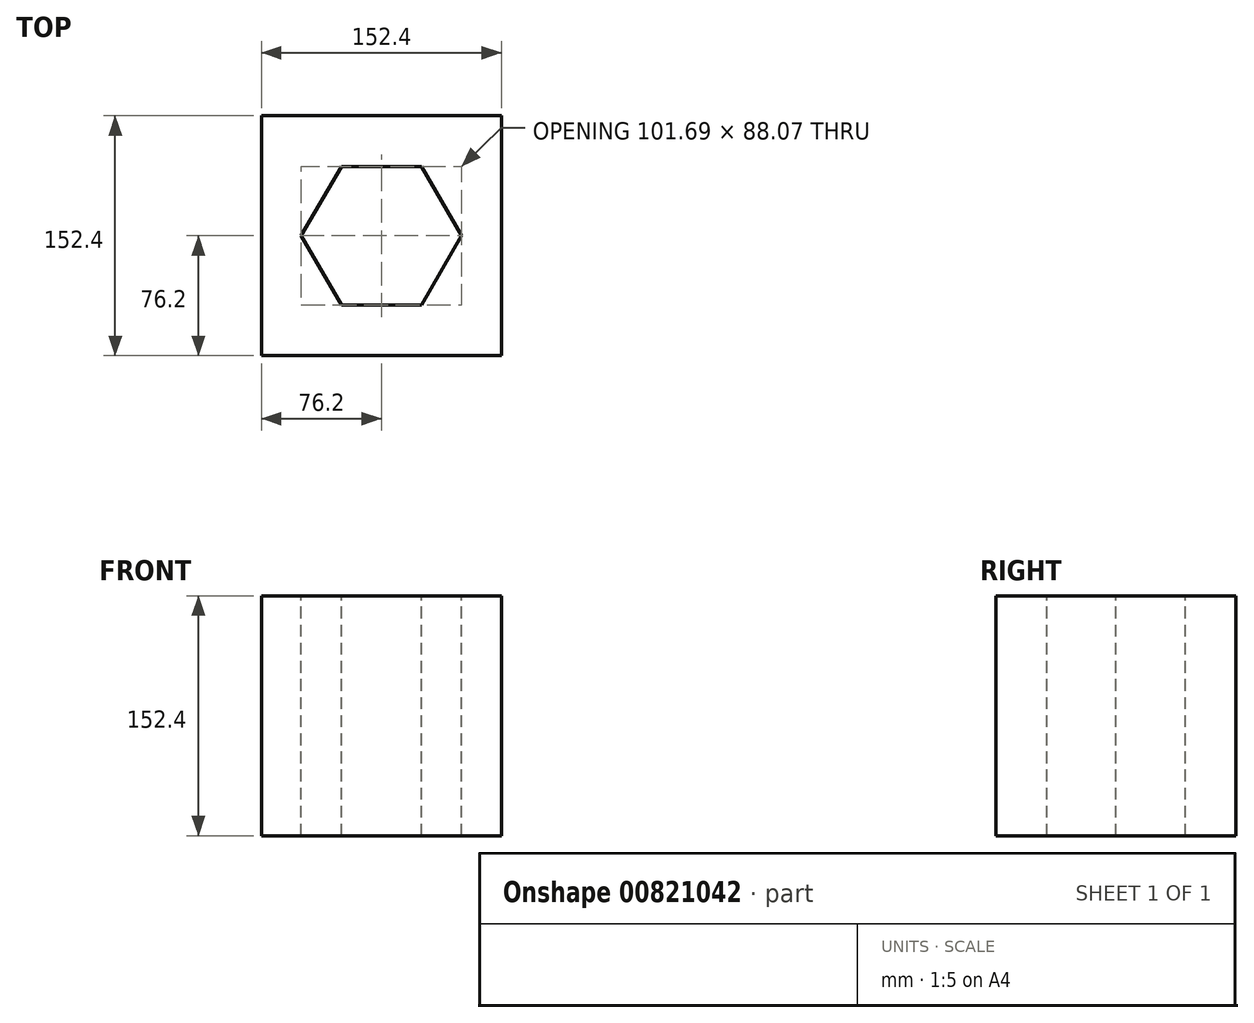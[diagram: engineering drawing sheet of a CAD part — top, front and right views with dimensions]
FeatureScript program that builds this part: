
annotation { "Feature Type Name" : "Feature", "Feature Type Description" : "" }
export const myFeature = defineFeature(function(context is Context, id is Id, definition is map)
    precondition{}
    {
        {
            var Q0;
            Q0=qCreatedBy(makeId("Top.planeOp"),FACE);
            var sketch = newSketch(context, id + "F0", { "sketchPlane" : qUnion([Q0])});
            skLineSegment(sketch, "E0.bottom", {"start": v(-76.2, 76.2) * mm, "end": v(76.2, 76.2) * mm});
            skLineSegment(sketch, "E0.top", {"start": v(-76.2, -76.2) * mm, "end": v(76.2, -76.2) * mm});
            skLineSegment(sketch, "E0.left", {"start": v(-76.2, 76.2) * mm, "end": v(-76.2, -76.2) * mm});
            skLineSegment(sketch, "E0.right", {"start": v(76.2, 76.2) * mm, "end": v(76.2, -76.2) * mm});
            skPoint(sketch, "E0.middle", {"position": v(0, 0) * mm});
            skSolve(sketch);
        }
        {
            var Q0;
            Q0=makeQuery(id+"F0.imprint","IMPRINT",FACE,{"disambiguationData":[TD([[makeQuery(id+"F0.imprint","IMPRINT",EDGE,{"derivedFrom":sQuery(id+"F0.wireOp",EDGE,"E0.bottom")}),-1.0]])]});
            extrude(context, id + "F1", {"entities" : qUnion([Q0]), "depth" : 152.4 * mm, "offsetDistance" : 25.4 * mm});
        }
        {
            var Q0;
            Q0=makeQuery(id+"F1.opExtrude","CAP_FACE",FACE,{"disambiguationData":[OSD([sQuery(id+"F0.wireOp",EDGE,"E0.bottom"),sQuery(id+"F0.wireOp",EDGE,"E0.top"),sQuery(id+"F0.wireOp",EDGE,"E0.left"),sQuery(id+"F0.wireOp",EDGE,"E0.right")])],"isStart":false});
            var sketch = newSketch(context, id + "F2", { "sketchPlane" : qUnion([Q0])});
            skCircle(sketch, "E1.cCircle", {"center": v(0, 0) * mm, "radius": 44.03 * mm, "construction": true});
            skLineSegment(sketch, "E1.0", {"start": v(-50.85, 0) * mm, "end": v(-25.42, 44.03) * mm});
            skLineSegment(sketch, "E1.1", {"start": v(-25.42, 44.03) * mm, "end": v(25.42, 44.03) * mm});
            skLineSegment(sketch, "E1.2", {"start": v(25.42, 44.03) * mm, "end": v(50.85, 0) * mm});
            skLineSegment(sketch, "E1.3", {"start": v(50.85, 0) * mm, "end": v(25.42, -44.03) * mm});
            skLineSegment(sketch, "E1.4", {"start": v(25.42, -44.03) * mm, "end": v(-25.42, -44.03) * mm});
            skLineSegment(sketch, "E1.5", {"start": v(-25.42, -44.03) * mm, "end": v(-50.85, 0) * mm});
            skPoint(sketch, "E1.0.midPoint", {"position": v(-38.13, 22.02) * mm});
            skSolve(sketch);
        }
        {
            var Q0;
            Q0=makeQuery(id+"F2.imprint","IMPRINT",FACE,{"disambiguationData":[TD([[makeQuery(id+"F2.imprint","IMPRINT",EDGE,{"derivedFrom":sQuery(id+"F2.wireOp",EDGE,"E1.0")}),-1.0]])]});
            extrude(context, id + "F3", {"entities" : qUnion([Q0]), "operationType" : NewBodyOperationType.REMOVE, "oppositeDirection" : true, "depth" : 152.4 * mm, "offsetDistance" : 25.4 * mm});
        }
    });
